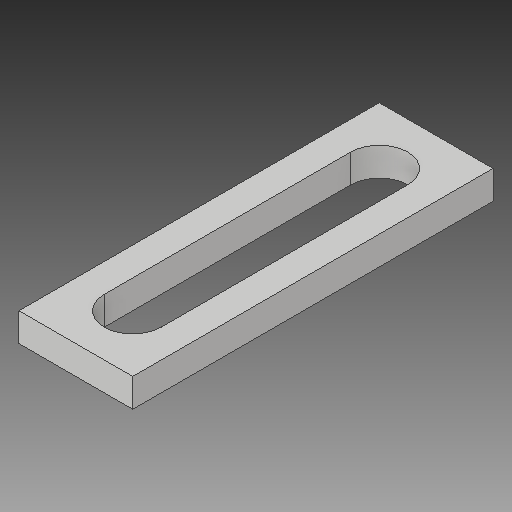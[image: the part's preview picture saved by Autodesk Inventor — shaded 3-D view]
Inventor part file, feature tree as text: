
AUTODESK INVENTOR PART (.ipt)
format: ipt  version: 2017 (Build 210142000, 142)  size: 110,080 bytes
history: native  units: in
note: dims shown in document units (in); Inventor stores cm internally (conversion verified against a paired STEP export)
features: extrude x2, sketch x2, projected_geometry x1
ambient origin geometry x8: Origin, YZ Plane, XZ Plane, XY Plane, X Axis, Y Axis, Z Axis, Center Point
bodies: Solid1 (feature_tree)
feature tree (5):
  extrude  "Extrusion1"  Depth=9.5in
  extrude  "Extrusion3"  Depth=0.75in
  sketch  "Sketch1"  dims[d0=3.0in d1=9.5in]
  sketch  "Sketch3"  dims[d2=0.75in d3=0.0in d11=0.75in d12=0.75in d13=1.0in d14=0.0in]
  projected_geometry  "Projected Loop2"
